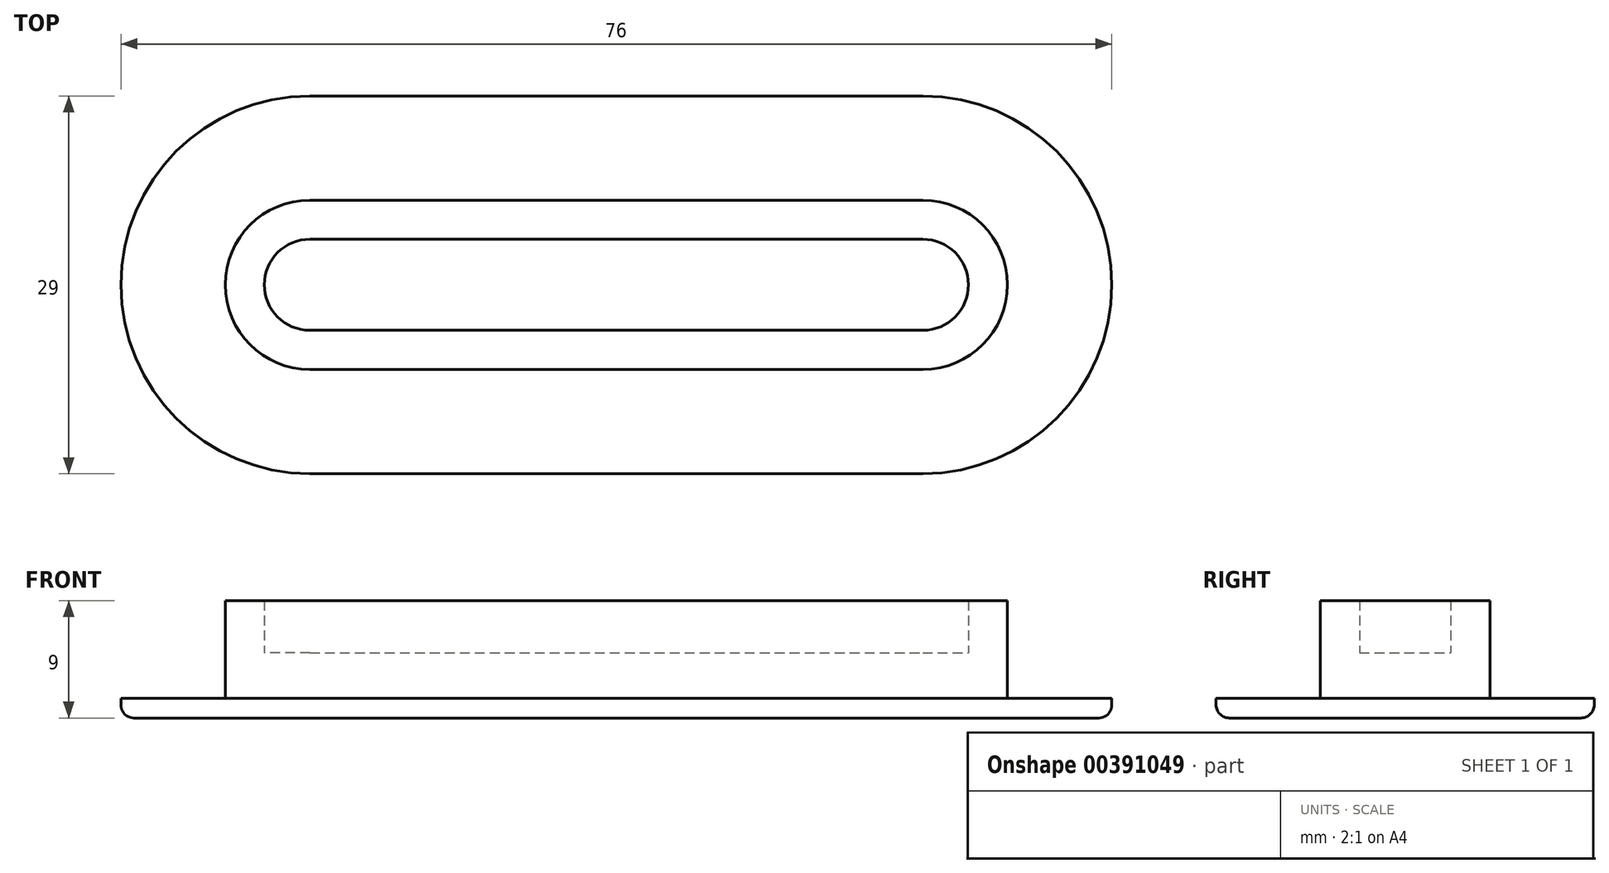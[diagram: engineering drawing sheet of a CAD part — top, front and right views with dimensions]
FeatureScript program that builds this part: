
annotation { "Feature Type Name" : "Feature", "Feature Type Description" : "" }
export const myFeature = defineFeature(function(context is Context, id is Id, definition is map)
    precondition{}
    {
        {
            var Q0;
            Q0=qCreatedBy(makeId("Top.planeOp"),FACE);
            var sketch = newSketch(context, id + "F0", { "sketchPlane" : qUnion([Q0])});
            skLineSegment(sketch, "E0.bottom", {"start": v(23.5, -14.5) * mm, "end": v(-23.5, -14.5) * mm});
            skLineSegment(sketch, "E0.top", {"start": v(23.5, 14.5) * mm, "end": v(-23.5, 14.5) * mm});
            skLineSegment(sketch, "E0.left", {"start": v(23.5, -14.5) * mm, "end": v(23.5, 14.5) * mm});
            skLineSegment(sketch, "E0.right", {"start": v(-23.5, -14.5) * mm, "end": v(-23.5, 14.5) * mm});
            skPoint(sketch, "E0.middle", {"position": v(0, 0) * mm});
            skArc(sketch, "E1", {"start": v(-23.5, 14.5) * mm, "mid": v(-38, 0) * mm, "end": v(-23.5, -14.5) * mm});
            skArc(sketch, "E2", {"start": v(23.5, -14.5) * mm, "mid": v(38, 0) * mm, "end": v(23.5, 14.5) * mm});
            skSolve(sketch);
        }
        {
            var Q0;
            Q0 = qSketchRegion(id + "F0", true);
            extrude(context, id + "F1", {"entities" : qUnion([Q0]), "depth" : 1.5 * mm});
        }
        {
            var Q0;
            Q0 = qSketchRegion(id + "F0", true);
            var sketch = newSketch(context, id + "F2", { "sketchPlane" : qUnion([Q0])});
            skLineSegment(sketch, "E3.bottom", {"start": v(23.5, -6.5) * mm, "end": v(-23.5, -6.5) * mm});
            skLineSegment(sketch, "E3.top", {"start": v(23.5, 6.5) * mm, "end": v(-23.5, 6.5) * mm});
            skLineSegment(sketch, "E3.left", {"start": v(23.5, -6.5) * mm, "end": v(23.5, 6.5) * mm});
            skLineSegment(sketch, "E3.right", {"start": v(-23.5, -6.5) * mm, "end": v(-23.5, 6.5) * mm});
            skPoint(sketch, "E3.middle", {"position": v(0, 0) * mm});
            skArc(sketch, "E4", {"start": v(-23.5, 6.5) * mm, "mid": v(-30, 0) * mm, "end": v(-23.5, -6.5) * mm});
            skArc(sketch, "E5", {"start": v(23.5, -6.5) * mm, "mid": v(30, 0) * mm, "end": v(23.5, 6.5) * mm});
            skSolve(sketch);
        }
        {
            var Q0;
            Q0 = qSketchRegion(id + "F2", true);
            extrude(context, id + "F3", {"entities" : qUnion([Q0]), "operationType" : NewBodyOperationType.ADD, "depth" : 9 * mm});
        }
        {
            var Q0;
            Q0=makeQuery(id+"F3.opExtrude","CAP_FACE",FACE,{"disambiguationData":[OSD([sQuery(id+"F2.wireOp",EDGE,"E3.bottom"),sQuery(id+"F2.wireOp",EDGE,"E3.top"),sQuery(id+"F2.wireOp",EDGE,"E4"),sQuery(id+"F2.wireOp",EDGE,"E5")])],"isStart":false});
            shell(context, id + "F4", {"entities" : qUnion([Q0]), "thickness" : 3 * mm});
        }
        {
            var Q0;
            Q0=makeQuery(id+"F1.opExtrude","CAP_EDGE",EDGE,{"disambiguationData":[OSD([sQuery(id+"F0.wireOp",EDGE,"E2")])],"isStart":true});
            var Q1;
            Q1=makeQuery(id+"F1.opExtrude","CAP_EDGE",EDGE,{"disambiguationData":[OSD([sQuery(id+"F0.wireOp",EDGE,"E0.bottom")])],"isStart":true});
            var Q2;
            Q2=makeQuery(id+"F1.opExtrude","CAP_EDGE",EDGE,{"disambiguationData":[OSD([sQuery(id+"F0.wireOp",EDGE,"E1")])],"isStart":true});
            var Q3;
            Q3=makeQuery(id+"F1.opExtrude","CAP_EDGE",EDGE,{"disambiguationData":[OSD([sQuery(id+"F0.wireOp",EDGE,"E0.top")])],"isStart":true});
            fillet(context, id + "F5", {"entities" : qUnion([Q0, Q1, Q2, Q3]), "radius" : 1 * mm, "tangentPropagation" : true, "allowEdgeOverflow" : false});
        }
        {
            var Q0;
            Q0=makeQuery(id+"F4.opShell","OFFSET_FACE",FACE,{"disambiguationData":[OSD([sQuery(id+"F0.wireOp",EDGE,"E0.bottom"),sQuery(id+"F0.wireOp",EDGE,"E0.top"),sQuery(id+"F0.wireOp",EDGE,"E1"),sQuery(id+"F0.wireOp",EDGE,"E2")])]});
            extrude(context, id + "F6", {"entities" : qUnion([Q0]), "operationType" : NewBodyOperationType.ADD, "depth" : 2 * mm});
        }
    });
